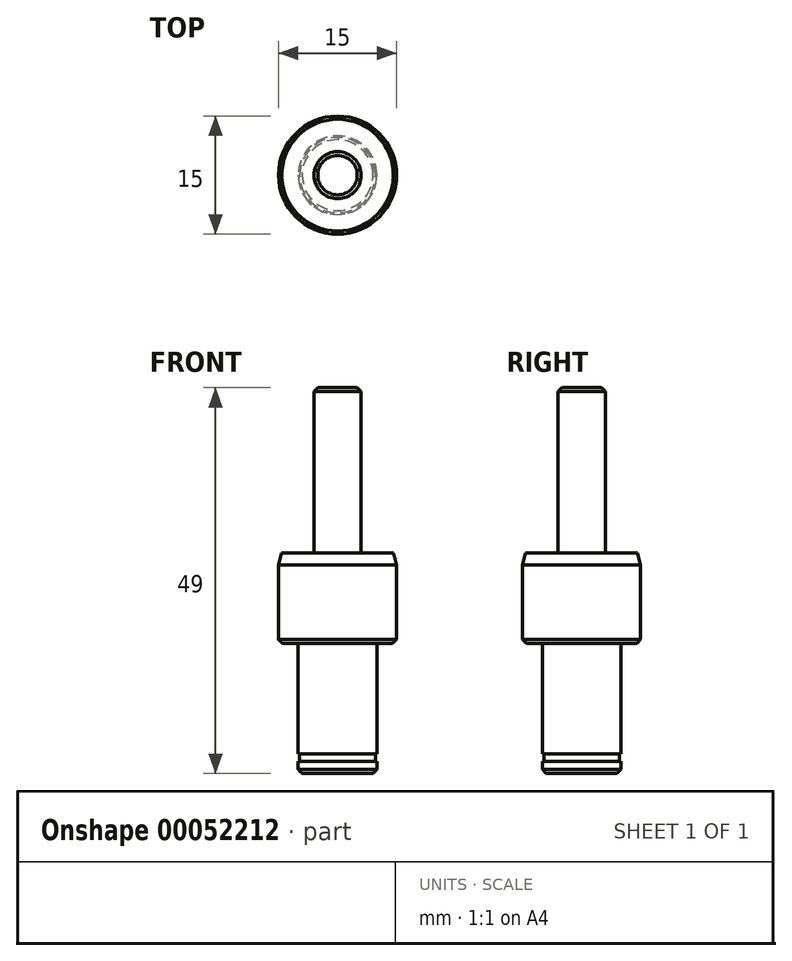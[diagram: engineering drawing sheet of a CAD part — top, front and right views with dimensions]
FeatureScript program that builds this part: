
annotation { "Feature Type Name" : "Feature", "Feature Type Description" : "" }
export const myFeature = defineFeature(function(context is Context, id is Id, definition is map)
    precondition{}
    {
        {
            var Q0;
            Q0=qCreatedBy(makeId("Front.planeOp"),FACE);
            var sketch = newSketch(context, id + "F0", { "sketchPlane" : qUnion([Q0])});
            skLineSegment(sketch, "E0", {"start": v(0, 49.2) * mm, "end": v(0, -58.86) * mm, "construction": true});
            skLineSegment(sketch, "E1", {"start": v(0, 32.5) * mm, "end": v(3, 32.5) * mm});
            skLineSegment(sketch, "E2", {"start": v(3, 32.5) * mm, "end": v(3, 11.5) * mm});
            skLineSegment(sketch, "E3", {"start": v(3, 11.5) * mm, "end": v(7.5, 11.5) * mm});
            skLineSegment(sketch, "E4", {"start": v(7.5, 11.5) * mm, "end": v(7.5, 0) * mm});
            skLineSegment(sketch, "E5", {"start": v(7.5, 0) * mm, "end": v(5, 0) * mm});
            skLineSegment(sketch, "E6", {"start": v(5, 0) * mm, "end": v(5, -14) * mm});
            skLineSegment(sketch, "E7", {"start": v(5, -14) * mm, "end": v(4.8, -14) * mm});
            skLineSegment(sketch, "E8", {"start": v(4.8, -14) * mm, "end": v(4.8, -15) * mm});
            skLineSegment(sketch, "E9", {"start": v(4.8, -15) * mm, "end": v(5, -15) * mm});
            skLineSegment(sketch, "E10", {"start": v(5, -15) * mm, "end": v(5, -16.5) * mm});
            skLineSegment(sketch, "E11", {"start": v(5, -16.5) * mm, "end": v(0, -16.5) * mm});
            skLineSegment(sketch, "E12", {"start": v(0, -16.5) * mm, "end": v(0, 32.5) * mm});
            skSolve(sketch);
        }
        {
            var Q0;
            Q0=makeQuery(id+"F0.imprint","IMPRINT",FACE,{"disambiguationData":[TD([[makeQuery(id+"F0.imprint","IMPRINT",EDGE,{"derivedFrom":sQuery(id+"F0.wireOp",EDGE,"E1")}),-1.0]])]});
            var Q1;
            Q1=sQuery(id+"F0.wireOp",EDGE,"E0");
            revolve(context, id + "F1", {"entities" : qUnion([Q0]), "axis" : qUnion([Q1]), "revolveType" : RevolveType.FULL});
        }
        {
            var Q0;
            Q0=makeQuery(id+"F1.opRevolve","SWEPT_EDGE",EDGE,{"disambiguationData":[OSD([sQuery(id+"F0.wireOp",EDGE,"E10"),sQuery(id+"F0.wireOp",EDGE,"E11")])]});
            var Q1;
            Q1=makeQuery(id+"F1.opRevolve","SWEPT_EDGE",EDGE,{"disambiguationData":[OSD([sQuery(id+"F0.wireOp",EDGE,"E1"),sQuery(id+"F0.wireOp",EDGE,"E2")])]});
            var Q2;
            Q2=makeQuery(id+"F1.opRevolve","SWEPT_EDGE",EDGE,{"disambiguationData":[OSD([sQuery(id+"F0.wireOp",EDGE,"E4"),sQuery(id+"F0.wireOp",EDGE,"E5")])]});
            chamfer(context, id + "F2", {"entities" : qUnion([Q0, Q1, Q2]), "width" : 0.5 * mm, "tangentPropagation" : true});
        }
        {
            var Q0;
            Q0=makeQuery(id+"F1.opRevolve","SWEPT_EDGE",EDGE,{"disambiguationData":[OSD([sQuery(id+"F0.wireOp",EDGE,"E5"),sQuery(id+"F0.wireOp",EDGE,"E6")])]});
            var Q1;
            Q1=makeQuery(id+"F1.opRevolve","SWEPT_EDGE",EDGE,{"disambiguationData":[OSD([sQuery(id+"F0.wireOp",EDGE,"E2"),sQuery(id+"F0.wireOp",EDGE,"E3")])]});
            fillet(context, id + "F3", {"entities" : qUnion([Q0, Q1]), "radius" : 0.1 * mm, "tangentPropagation" : true, "allowEdgeOverflow" : false});
        }
        {
            var Q0;
            Q0=makeQuery(id+"F1.opRevolve","SWEPT_EDGE",EDGE,{"disambiguationData":[OSD([sQuery(id+"F0.wireOp",EDGE,"E3"),sQuery(id+"F0.wireOp",EDGE,"E4")])]});
            chamfer(context, id + "F4", {"entities" : qUnion([Q0]), "chamferType" : ChamferType.OFFSET_ANGLE, "width" : 1.5 * mm, "oppositeDirection" : true, "angle" : 15 * degree, "tangentPropagation" : true});
        }
    });
